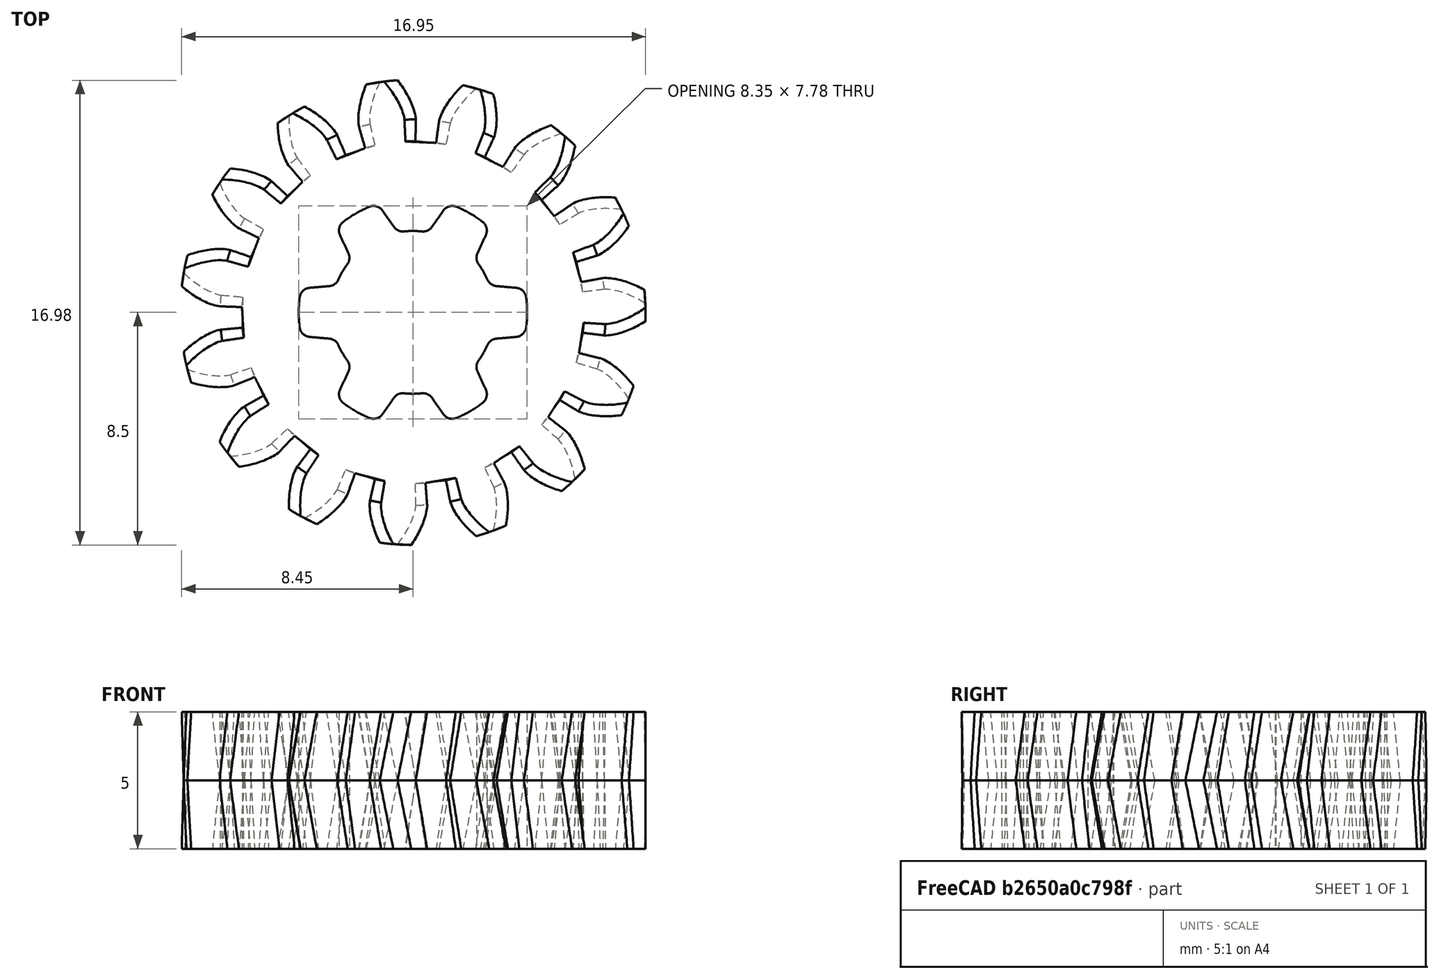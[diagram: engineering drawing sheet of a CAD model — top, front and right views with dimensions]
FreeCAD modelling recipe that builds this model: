
FCSTD DOCUMENT  (FreeCAD 0.21R33771 (Git))
Label: shevronnaja_shesternja2
License: All rights reserved
LicenseURL: https://en.wikipedia.org/wiki/All_rights_reserved
objects: PartDesign::FeaturePython×2, Sketcher::SketchObject×1, PartDesign::Pocket×1, PartDesign::Body×1
note: 6 computed .brp shape members not serialized (recipe doc carries the construction recipe); baked Part::Feature solids carry a one-line shape summary decoded from their .brp

FEATURE [PartDesign::FeaturePython] InvoluteGear  # WARN: FeaturePython — macro-defined, semantics opaque (R4)
  AttacherType = Attacher::AttachEngine3D
  angular_backlash = 0
  backlash = 0
  beta = 10
  clearance = 0.25
  da = 17
  df = 12.5
  double_helix = true
  dw = 15
  head = 0
  head_fillet = 0
  height = 5
  module = 1
  numpoints = 20
  pressure_angle = 20
  properties_from_tool = false
  reversed_backlash = false
  root_fillet = 0
  shift = 0
  simple = false
  teeth = 15
  transverse_pitch = 3.14159
  traverse_module = 1
  undercut = false
  version = 1.2.0
  expr: angular_backlash = backlash / dw * 360 ° / pi
FEATURE [Sketcher::SketchObject] Sketch
  FullyConstrained = true
  MapMode = 5
  Placement = pos=(-1.50458e-05,-8.85248e-07,4.99997) rot=(0.058738,-0.998317,0;3e-06rad)
  Support = -> [InvoluteGear]
FEATURE [PartDesign::FeaturePython] TimingGearT  # WARN: FeaturePython — macro-defined, semantics opaque (R4)
  AttacherType = Attacher::AttachEngine3D
  BaseFeature = -> InvoluteGear
  alpha = 40
  backlash = 0
  head_fillet = 0.4
  height = 5
  pitch = 5
  root_fillet = 0.4
  teeth = 6
  tooth_height = 1.2
  u = 0.6
FEATURE [PartDesign::Pocket] Pocket
  BaseFeature = -> TimingGearT
  Direction = (0,0,-1)
  Length = 5
  Length2 = 5
  Profile = -> TimingGearT [Face279]
  Type = 0
FEATURE [PartDesign::Body] Body
  Group = -> [InvoluteGear,Sketch,TimingGearT,Pocket]
  Origin = -> Origin
  Tip = -> Pocket
